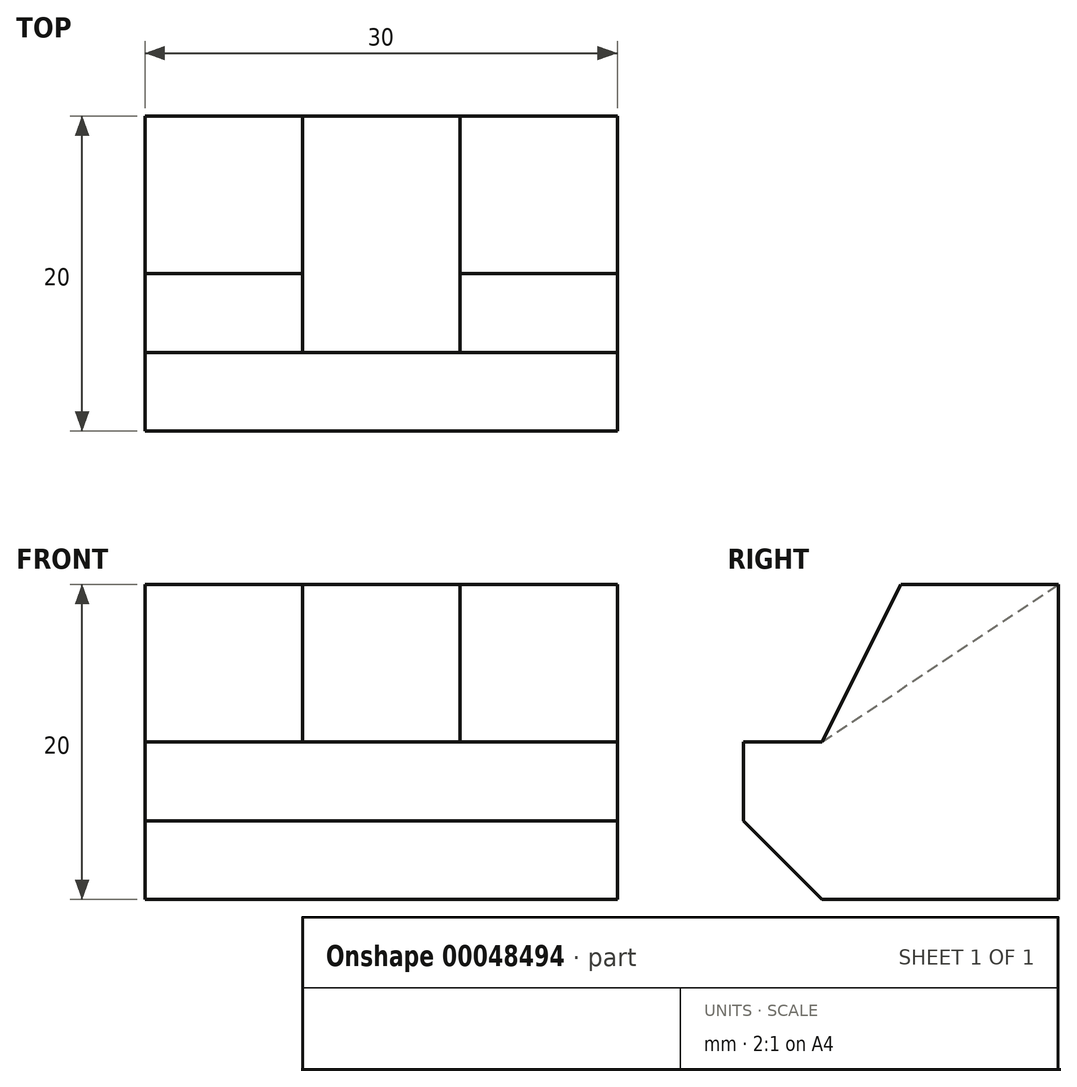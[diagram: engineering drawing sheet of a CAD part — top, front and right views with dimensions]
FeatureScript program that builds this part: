
annotation { "Feature Type Name" : "Feature", "Feature Type Description" : "" }
export const myFeature = defineFeature(function(context is Context, id is Id, definition is map)
    precondition{}
    {
        {
            var Q0;
            Q0=qCreatedBy(makeId("Right.planeOp"),FACE);
            var sketch = newSketch(context, id + "F0", { "sketchPlane" : qUnion([Q0])});
            skLineSegment(sketch, "E0", {"start": v(0, 0) * mm, "end": v(15, 0) * mm});
            skLineSegment(sketch, "E1", {"start": v(15, 0) * mm, "end": v(15, 20) * mm});
            skLineSegment(sketch, "E2", {"start": v(15, 20) * mm, "end": v(5, 20) * mm});
            skLineSegment(sketch, "E3", {"start": v(5, 20) * mm, "end": v(0, 10) * mm});
            skLineSegment(sketch, "E4", {"start": v(0, 10) * mm, "end": v(-5, 10) * mm});
            skLineSegment(sketch, "E5", {"start": v(-5, 10) * mm, "end": v(-5, 5) * mm});
            skLineSegment(sketch, "E6", {"start": v(-5, 5) * mm, "end": v(0, 0) * mm});
            skSolve(sketch);
        }
        {
            var Q0;
            Q0=makeQuery(id+"F0.imprint","IMPRINT",FACE,{"disambiguationData":[TD([[makeQuery(id+"F0.imprint","IMPRINT",EDGE,{"derivedFrom":sQuery(id+"F0.wireOp",EDGE,"E0")}),1.0]])]});
            extrude(context, id + "F1", {"entities" : qUnion([Q0]), "depth" : 30 * mm});
        }
        {
            var Q0;
            Q0=makeQuery(id+"F1.opExtrude","CAP_VERTEX",VERTEX,{"disambiguationData":[OSD([sQuery(id+"F0.wireOp",EDGE,"E1"),sQuery(id+"F0.wireOp",EDGE,"E2")])],"isStart":true});
            var Q1;
            Q1=makeQuery(id+"F1.opExtrude","CAP_VERTEX",VERTEX,{"disambiguationData":[OSD([sQuery(id+"F0.wireOp",EDGE,"E1"),sQuery(id+"F0.wireOp",EDGE,"E2")])],"isStart":false});
            var Q2;
            Q2=makeQuery(id+"F1.opExtrude","CAP_VERTEX",VERTEX,{"disambiguationData":[OSD([sQuery(id+"F0.wireOp",EDGE,"E3"),sQuery(id+"F0.wireOp",EDGE,"E4")])],"isStart":false});
            cPlane(context, id + "F2", {"entities" : qUnion([Q0, Q1, Q2]), "cplaneType" : CPlaneType.THREE_POINT, "offset" : 150 * mm, "width" : 150 * mm, "height" : 150 * mm});
        }
        {
            var Q0;
            Q0=qCreatedBy(id+"F2.planeOp",FACE);
            var sketch = newSketch(context, id + "F3", { "sketchPlane" : qUnion([Q0])});
            skLineSegment(sketch, "E7", {"start": v(10, 23.57) * mm, "end": v(20, 23.57) * mm});
            skLineSegment(sketch, "E8", {"start": v(20, 23.57) * mm, "end": v(20, 5.55) * mm});
            skLineSegment(sketch, "E9", {"start": v(20, 5.55) * mm, "end": v(10, 5.55) * mm});
            skLineSegment(sketch, "E10", {"start": v(10, 5.55) * mm, "end": v(10, 23.57) * mm});
            skSolve(sketch);
        }
        {
            var Q0;
            Q0 = qSketchRegion(id + "F3", true);
            extrude(context, id + "F4", {"entities" : qUnion([Q0]), "operationType" : NewBodyOperationType.REMOVE, "endBound" : BoundingType.THROUGH_ALL, "depth" : 25 * mm});
        }
    });
